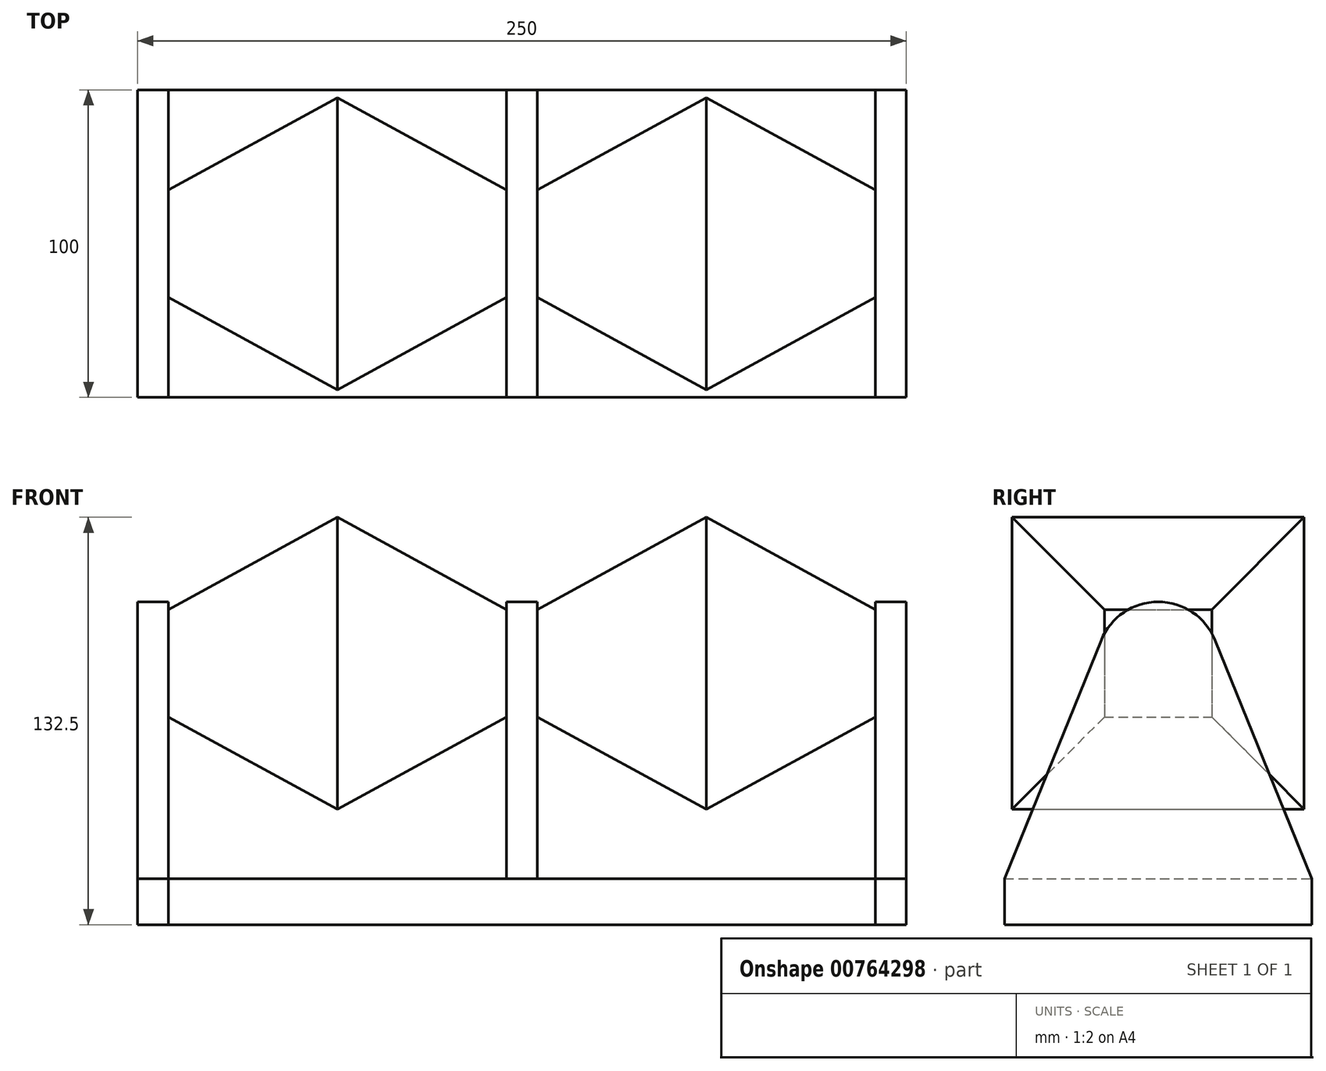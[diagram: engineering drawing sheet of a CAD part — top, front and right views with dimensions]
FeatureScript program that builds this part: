
annotation { "Feature Type Name" : "Feature", "Feature Type Description" : "" }
export const myFeature = defineFeature(function(context is Context, id is Id, definition is map)
    precondition{}
    {
        {
            assignVariable(context, id + "F0", {"name" : "breite", "anyValue" : 110});
        }
        {
            assignVariable(context, id + "F1", {"name" : "hoehe", "anyValue" : 95});
        }
        {
            var Q0;
            Q0=qCreatedBy(makeId("Front.planeOp"),FACE);
            var sketch = newSketch(context, id + "F2", { "sketchPlane" : qUnion([Q0])});
            skLineSegment(sketch, "E0", {"start": v(-55, 17.5) * mm, "end": v(0, 47.5) * mm});
            skLineSegment(sketch, "E1", {"start": v(0, 47.5) * mm, "end": v(55, 17.5) * mm});
            skLineSegment(sketch, "E2", {"start": v(55, 17.5) * mm, "end": v(55, -17.5) * mm});
            skLineSegment(sketch, "E3", {"start": v(55, -17.5) * mm, "end": v(0, -47.5) * mm});
            skLineSegment(sketch, "E4", {"start": v(0, -47.5) * mm, "end": v(-55, -17.5) * mm});
            skLineSegment(sketch, "E5", {"start": v(-55, -17.5) * mm, "end": v(-55, 17.5) * mm});
            skLineSegment(sketch, "E6", {"start": v(0, 0) * mm, "end": v(-55, 0) * mm, "construction": true});
            skSolve(sketch);
        }
        {
            var Q0;
            Q0=makeQuery(id+"F2.imprint","IMPRINT",FACE,{"disambiguationData":[TD([[makeQuery(id+"F2.imprint","IMPRINT",EDGE,{"derivedFrom":sQuery(id+"F2.wireOp",EDGE,"E0")}),-1.0]])]});
            extrude(context, id + "F3", {"entities" : qUnion([Q0]), "endBound" : BoundingType.SYMMETRIC, "depth" : (getVariable(context, 'hoehe')) * mm, "offsetDistance" : 25 * mm});
        }
        {
            var Q0;
            Q0=qCreatedBy(makeId("Top.planeOp"),FACE);
            var sketch = newSketch(context, id + "F4", { "sketchPlane" : qUnion([Q0])});
            skLineSegment(sketch, "E7", {"start": v(0, 47.5) * mm, "end": v(-55, 17.5) * mm});
            skLineSegment(sketch, "E8", {"start": v(-55, 17.5) * mm, "end": v(-55, -17.5) * mm});
            skLineSegment(sketch, "E9", {"start": v(-55, -17.5) * mm, "end": v(0, -47.5) * mm});
            skLineSegment(sketch, "E10", {"start": v(0, -47.5) * mm, "end": v(55, -17.5) * mm});
            skLineSegment(sketch, "E11", {"start": v(55, -17.5) * mm, "end": v(55, 17.5) * mm});
            skLineSegment(sketch, "E12", {"start": v(55, 17.5) * mm, "end": v(0, 47.5) * mm});
            skLineSegment(sketch, "E13", {"start": v(-55, 17.5) * mm, "end": v(-55, 47.5) * mm});
            skLineSegment(sketch, "E14", {"start": v(-55, 47.5) * mm, "end": v(0, 47.5) * mm});
            skLineSegment(sketch, "E15", {"start": v(0, 47.5) * mm, "end": v(55, 47.5) * mm});
            skLineSegment(sketch, "E16", {"start": v(55, 47.5) * mm, "end": v(55, 17.5) * mm});
            skLineSegment(sketch, "E17", {"start": v(55, -17.5) * mm, "end": v(55, -47.5) * mm});
            skLineSegment(sketch, "E18", {"start": v(55, -47.5) * mm, "end": v(0, -47.5) * mm});
            skLineSegment(sketch, "E19", {"start": v(-55, -17.5) * mm, "end": v(-55, -47.5) * mm});
            skLineSegment(sketch, "E20", {"start": v(-55, -47.5) * mm, "end": v(0, -47.5) * mm});
            skSolve(sketch);
        }
        {
            var Q0;
            Q0=makeQuery(id+"F4.imprint","IMPRINT",FACE,{"disambiguationData":[TD([[makeQuery(id+"F4.imprint","IMPRINT",EDGE,{"derivedFrom":sQuery(id+"F4.wireOp",EDGE,"E7")}),-1.0]])]});
            var Q1;
            Q1=makeQuery(id+"F4.imprint","IMPRINT",FACE,{"disambiguationData":[TD([[makeQuery(id+"F4.imprint","IMPRINT",EDGE,{"derivedFrom":sQuery(id+"F4.wireOp",EDGE,"E12")}),-1.0]])]});
            var Q2;
            Q2=makeQuery(id+"F4.imprint","IMPRINT",FACE,{"disambiguationData":[TD([[makeQuery(id+"F4.imprint","IMPRINT",EDGE,{"derivedFrom":sQuery(id+"F4.wireOp",EDGE,"E10")}),-1.0]])]});
            var Q3;
            Q3=makeQuery(id+"F4.imprint","IMPRINT",FACE,{"disambiguationData":[TD([[makeQuery(id+"F4.imprint","IMPRINT",EDGE,{"derivedFrom":sQuery(id+"F4.wireOp",EDGE,"E9")}),-1.0]])]});
            extrude(context, id + "F5", {"entities" : qUnion([Q0, Q1, Q2, Q3]), "operationType" : NewBodyOperationType.REMOVE, "endBound" : BoundingType.SYMMETRIC, "depth" : (getVariable(context, 'breite')) * mm, "offsetDistance" : 25 * mm});
        }
        {
            var Q0;
            Q0=makeQuery(id+"F3.opExtrude","SWEPT_FACE",FACE,{"disambiguationData":[OSD([sQuery(id+"F2.wireOp",EDGE,"E5")])]});
            var sketch = newSketch(context, id + "F6", { "sketchPlane" : qUnion([Q0])});
            skLineSegment(sketch, "E21", {"start": v(-50, -70) * mm, "end": v(-18.53, 7.52) * mm});
            skLineSegment(sketch, "E22", {"start": v(-50, -70) * mm, "end": v(50, -70) * mm});
            skLineSegment(sketch, "E23", {"start": v(50, -70) * mm, "end": v(18.53, 7.52) * mm});
            skArc(sketch, "E24", {"start": v(18.53, 7.52) * mm, "mid": v(0, 20) * mm, "end": v(-18.53, 7.52) * mm});
            skLineSegment(sketch, "E25", {"start": v(-50, -70) * mm, "end": v(-50, -85) * mm});
            skLineSegment(sketch, "E26", {"start": v(-50, -85) * mm, "end": v(50, -85) * mm});
            skLineSegment(sketch, "E27", {"start": v(50, -85) * mm, "end": v(50, -70) * mm});
            skSolve(sketch);
        }
        {
            var Q0;
            Q0 = qSketchRegion(id + "F6", true);
            extrude(context, id + "F7", {"entities" : qUnion([Q0]), "depth" : 10 * mm, "offsetDistance" : 25 * mm});
        }
        {
            var Q0;
            Q0=makeQuery(id+"F3.opExtrude","SWEPT_FACE",FACE,{"disambiguationData":[OSD([sQuery(id+"F2.wireOp",EDGE,"E2")])]});
            var sketch = newSketch(context, id + "F8", { "sketchPlane" : qUnion([Q0])});
            skLineSegment(sketch, "E28.0.0", {"start": v(50, -85) * mm, "end": v(-50, -85) * mm});
            skLineSegment(sketch, "E28.0.1", {"start": v(-50, -85) * mm, "end": v(-50, -70) * mm});
            skLineSegment(sketch, "E28.0.2", {"start": v(-50, -70) * mm, "end": v(-18.53, 7.52) * mm});
            skArc(sketch, "E28.0.3", {"start": v(-18.53, 7.52) * mm, "mid": v(0, 20) * mm, "end": v(18.53, 7.52) * mm});
            skLineSegment(sketch, "E28.0.4", {"start": v(18.53, 7.52) * mm, "end": v(50, -70) * mm});
            skLineSegment(sketch, "E28.0.5", {"start": v(50, -70) * mm, "end": v(50, -85) * mm});
            skSolve(sketch);
        }
        {
            var Q0;
            Q0 = qSketchRegion(id + "F8", true);
            extrude(context, id + "F9", {"entities" : qUnion([Q0]), "depth" : 5 * mm, "offsetDistance" : 25 * mm});
        }
        {
            var Q0;
            Q0=makeQuery(id+"F7.opExtrude","CAP_FACE",FACE,{"disambiguationData":[OSD([sQuery(id+"F6.wireOp",EDGE,"E21"),sQuery(id+"F6.wireOp",EDGE,"E23"),sQuery(id+"F6.wireOp",EDGE,"E24"),sQuery(id+"F6.wireOp",EDGE,"E25"),sQuery(id+"F6.wireOp",EDGE,"E26"),sQuery(id+"F6.wireOp",EDGE,"E27")])],"isStart":true});
            var sketch = newSketch(context, id + "F10", { "sketchPlane" : qUnion([Q0])});
            skLineSegment(sketch, "E29.bottom", {"start": v(-50, -85) * mm, "end": v(50, -85) * mm});
            skLineSegment(sketch, "E29.top", {"start": v(-50, -70) * mm, "end": v(50, -70) * mm});
            skLineSegment(sketch, "E29.left", {"start": v(-50, -85) * mm, "end": v(-50, -70) * mm});
            skLineSegment(sketch, "E29.right", {"start": v(50, -85) * mm, "end": v(50, -70) * mm});
            skSolve(sketch);
        }
        {
            var Q0;
            Q0=makeQuery(id+"F10.imprint","IMPRINT",FACE,{"disambiguationData":[TD([[makeQuery(id+"F10.imprint","IMPRINT",EDGE,{"derivedFrom":sQuery(id+"F10.wireOp",EDGE,"E29.bottom")}),-1.0]])]});
            extrude(context, id + "F11", {"entities" : qUnion([Q0]), "endBound" : BoundingType.UP_TO_NEXT, "depth" : 25 * mm, "offsetDistance" : 25 * mm});
        }
        {
            var Q0;
            Q0=makeQuery(id+"F3.opExtrude","SWEPT_BODY",BODY,{"disambiguationData":[OSD([sQuery(id+"F2.wireOp",EDGE,"E0"),sQuery(id+"F2.wireOp",EDGE,"E1"),sQuery(id+"F2.wireOp",EDGE,"E2"),sQuery(id+"F2.wireOp",EDGE,"E3"),sQuery(id+"F2.wireOp",EDGE,"E4"),sQuery(id+"F2.wireOp",EDGE,"E5")])]});
            var Q1;
            Q1=makeQuery(id+"F7.opExtrude","SWEPT_BODY",BODY,{"disambiguationData":[OSD([sQuery(id+"F6.wireOp",EDGE,"E21"),sQuery(id+"F6.wireOp",EDGE,"E23"),sQuery(id+"F6.wireOp",EDGE,"E24"),sQuery(id+"F6.wireOp",EDGE,"E25"),sQuery(id+"F6.wireOp",EDGE,"E26"),sQuery(id+"F6.wireOp",EDGE,"E27")])]});
            var Q2;
            Q2=makeQuery(id+"F11.opExtrude","SWEPT_BODY",BODY,{"disambiguationData":[OSD([sQuery(id+"F10.wireOp",EDGE,"E29.bottom"),sQuery(id+"F10.wireOp",EDGE,"E29.top"),sQuery(id+"F10.wireOp",EDGE,"E29.left"),sQuery(id+"F10.wireOp",EDGE,"E29.right")])]});
            var Q3;
            Q3=makeQuery(id+"F9.opExtrude","CAP_FACE",FACE,{"disambiguationData":[OSD([sQuery(id+"F8.wireOp",EDGE,"E28.0.0"),sQuery(id+"F8.wireOp",EDGE,"E28.0.1"),sQuery(id+"F8.wireOp",EDGE,"E28.0.2"),sQuery(id+"F8.wireOp",EDGE,"E28.0.3"),sQuery(id+"F8.wireOp",EDGE,"E28.0.4"),sQuery(id+"F8.wireOp",EDGE,"E28.0.5")])],"isStart":false});
            mirror(context, id + "F12", {"entities" : qUnion([Q0, Q1, Q2]), "mirrorPlane" : qUnion([Q3])});
        }
        {
            var Q0;
            Q0=makeQuery(id+"F9.opExtrude","SWEPT_BODY",BODY,{"disambiguationData":[OSD([sQuery(id+"F8.wireOp",EDGE,"E28.0.0"),sQuery(id+"F8.wireOp",EDGE,"E28.0.1"),sQuery(id+"F8.wireOp",EDGE,"E28.0.2"),sQuery(id+"F8.wireOp",EDGE,"E28.0.3"),sQuery(id+"F8.wireOp",EDGE,"E28.0.4"),sQuery(id+"F8.wireOp",EDGE,"E28.0.5")])]});
            var Q1;
            Q1=makeQuery(id+"F9.opExtrude","CAP_FACE",FACE,{"disambiguationData":[OSD([sQuery(id+"F8.wireOp",EDGE,"E28.0.0"),sQuery(id+"F8.wireOp",EDGE,"E28.0.1"),sQuery(id+"F8.wireOp",EDGE,"E28.0.2"),sQuery(id+"F8.wireOp",EDGE,"E28.0.3"),sQuery(id+"F8.wireOp",EDGE,"E28.0.4"),sQuery(id+"F8.wireOp",EDGE,"E28.0.5")])],"isStart":false});
            mirror(context, id + "F13", {"operationType" : NewBodyOperationType.ADD, "entities" : qUnion([Q0]), "mirrorPlane" : qUnion([Q1])});
        }
    });
